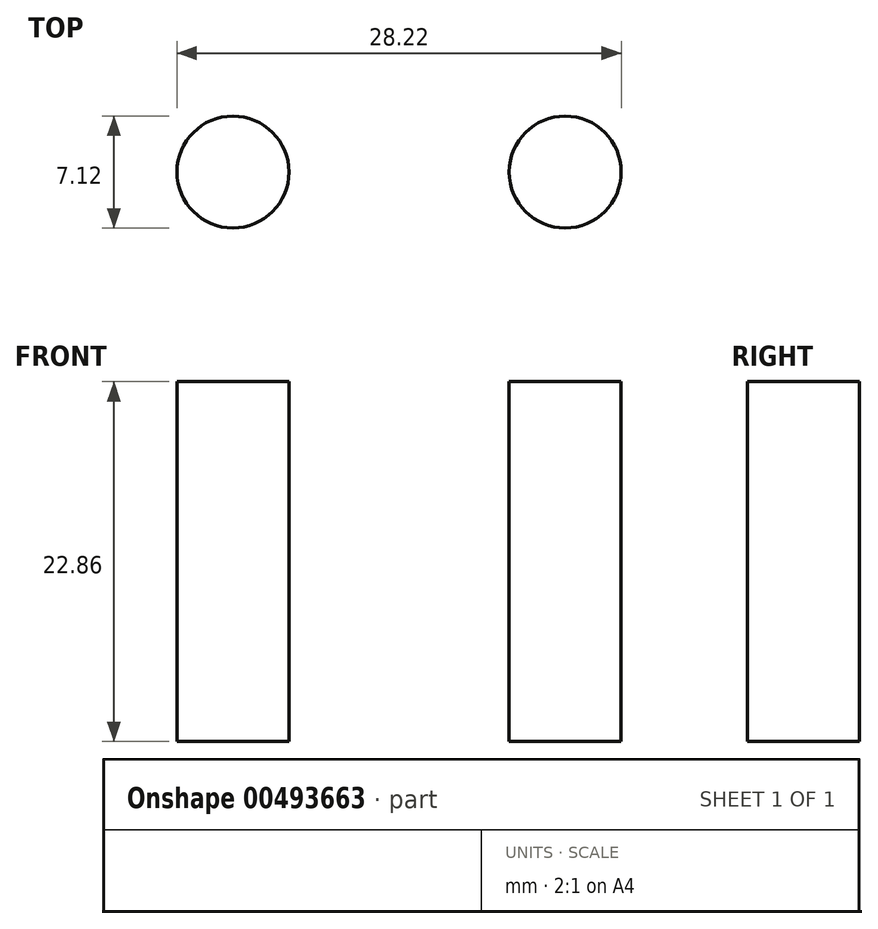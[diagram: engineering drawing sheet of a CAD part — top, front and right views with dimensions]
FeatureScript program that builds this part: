
annotation { "Feature Type Name" : "Feature", "Feature Type Description" : "" }
export const myFeature = defineFeature(function(context is Context, id is Id, definition is map)
    precondition{}
    {
        {
            var Q0;
            Q0=qCreatedBy(makeId("Top.planeOp"),FACE);
            var sketch = newSketch(context, id + "F0", { "sketchPlane" : qUnion([Q0])});
            skCircle(sketch, "E0", {"center": v(0, 0) * mm, "radius": 3.56 * mm});
            skCircle(sketch, "E1", {"center": v(-21.1, 0) * mm, "radius": 3.56 * mm});
            skSolve(sketch);
        }
        {
            var Q0;
            Q0 = qSketchRegion(id + "F0", true);
            extrude(context, id + "F1", {"entities" : qUnion([Q0]), "depth" : 22.86 * mm, "offsetDistance" : 25.4 * mm});
        }
    });
